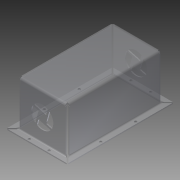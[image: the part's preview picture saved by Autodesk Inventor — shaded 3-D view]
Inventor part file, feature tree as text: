
AUTODESK INVENTOR PART (.ipt)
format: ipt  version: 2015 (Build 190159000, 159)  size: 488,448 bytes
history: native  units: in
note: dims shown in document units (in); Inventor stores cm internally (conversion verified against a paired STEP export)
features: sheet_metal_op x7, other x5, sketch x5, projected_geometry x5, extrude x1, fillet x1, hole x1
ambient origin geometry x8: Origin, YZ Plane, XZ Plane, XY Plane, X Axis, Y Axis, Z Axis, Center Point
bodies: Solid1 (feature_tree)
feature tree (25):
  sheet_metal_op  "Face1"
  sheet_metal_op  "Flange1"
  other  "A-Side Definition"
  sheet_metal_op  "Flange2"
  extrude  "Extrusion1"  Depth=0.125in
  fillet  "Fillet1"  Radius=0.125in
  hole  "Hole2"  [1 undecoded]
  sketch  "Sketch1"  dims[d0=5.0in d1=10.0in d2=0.125in]
  other  "Plate1"
  sketch  "Sketch2"  dims[d3=0.125in d4=0.0625in]
  other  "Plate2"
  sheet_metal_op  "Bend1"
  sheet_metal_op  "Corner1"
  sketch  "Sketch3"  dims[d5=0.25in]
  other  "Plate3"
  sheet_metal_op  "Bend2"
  sheet_metal_op  "Corner2"
  sketch  "Sketch5"  dims[d6=0.125in]
  projected_geometry  "Projected Loop5"
  sketch  "Sketch6"  dims[d7=5.0in d8=90.0deg d9=0.125in d10=0.5in d11=0.125in d12=0.125in d13=0.125in d14=0.0625in d15=0.25in d16=0.125in d17=0.75in d18=90.0deg d19=0.125in d20=0.5in d21=0.125in d22=0.125in d49=5.0in d50=4.625in d51=2.5in d52=2.3125in d53=2.3622in d54=1.0in d55=0.0in d56=0.9843in d57=0.1969in d58=1.5748in d60=360.0deg d62=0.125in d63=0.0625in d64=1.2205in d65=6.5732in d66=11.5732in d67=0.5in d68=0.25in d69=0.25in d70=0.25in d71=0.25in d72=2.1911in d73=2.1911in d74=3.8577in d75=3.8577in d76=3.8577in d77=3.8577in d78=2.1911in d79=2.1911in d80=0.266in d81=0.75in d82=0.438in d83=0.25in d84=0.5635in d85=0.125in d86=0.8108in]
  projected_geometry  "Projected Loop6"
  projected_geometry  "Projected Loop7"
  projected_geometry  "Projected Loop8"
  projected_geometry  "Projected Loop9"
  other  "Definition1"
note: 1 required parameter value undecoded (feature->parameter linkage not recoverable at this tier; creation-order binding heuristic only, values carry confidence <= 0.55)
